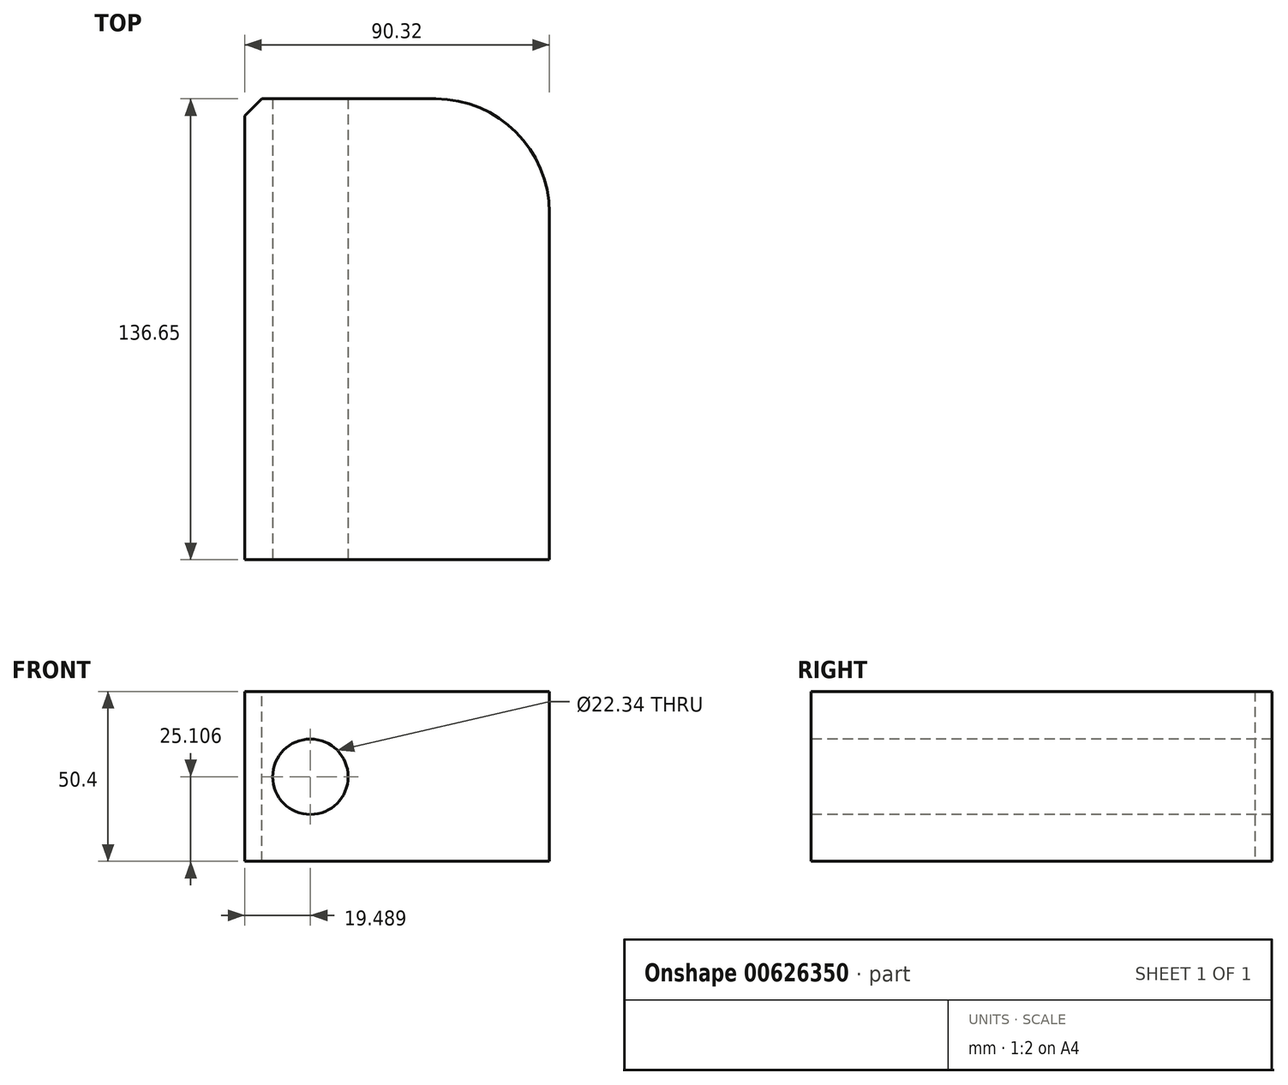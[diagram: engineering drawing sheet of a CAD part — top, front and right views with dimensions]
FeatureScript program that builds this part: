
annotation { "Feature Type Name" : "Feature", "Feature Type Description" : "" }
export const myFeature = defineFeature(function(context is Context, id is Id, definition is map)
    precondition{}
    {
        {
            var Q0;
            Q0=qCreatedBy(makeId("Front.planeOp"),FACE);
            var sketch = newSketch(context, id + "F0", { "sketchPlane" : qUnion([Q0])});
            skLineSegment(sketch, "E0.bottom", {"start": v(-47.97, 13.4) * mm, "end": v(42.35, 13.4) * mm});
            skLineSegment(sketch, "E0.top", {"start": v(-47.97, 63.8) * mm, "end": v(42.35, 63.8) * mm});
            skLineSegment(sketch, "E0.left", {"start": v(-47.97, 13.4) * mm, "end": v(-47.97, 63.8) * mm});
            skLineSegment(sketch, "E0.right", {"start": v(42.35, 13.4) * mm, "end": v(42.35, 63.8) * mm});
            skCircle(sketch, "E1", {"center": v(-28.48, 38.5) * mm, "radius": 11.17 * mm});
            skSolve(sketch);
        }
        {
            var Q0;
            Q0=makeQuery(id+"F0.imprint","IMPRINT",FACE,{"disambiguationData":[TD([[makeQuery(id+"F0.imprint","IMPRINT",EDGE,{"derivedFrom":sQuery(id+"F0.wireOp",EDGE,"E0.bottom")}),1.0]])]});
            extrude(context, id + "F1", {"entities" : qUnion([Q0]), "oppositeDirection" : true, "depth" : 136.65 * mm, "offsetDistance" : 25.4 * mm});
        }
        {
            var Q0;
            Q0=makeQuery(id+"F1.opExtrude","CAP_EDGE",EDGE,{"disambiguationData":[OSD([sQuery(id+"F0.wireOp",EDGE,"E0.right")])],"isStart":false});
            fillet(context, id + "F2", {"entities" : qUnion([Q0]), "radius" : 33.73 * mm, "tangentPropagation" : true, "allowEdgeOverflow" : false});
        }
        {
            var Q0;
            Q0=makeQuery(id+"F1.opExtrude","CAP_EDGE",EDGE,{"disambiguationData":[OSD([sQuery(id+"F0.wireOp",EDGE,"E0.left")])],"isStart":false});
            chamfer(context, id + "F3", {"entities" : qUnion([Q0]), "width" : 5.08 * mm, "tangentPropagation" : true});
        }
    });
